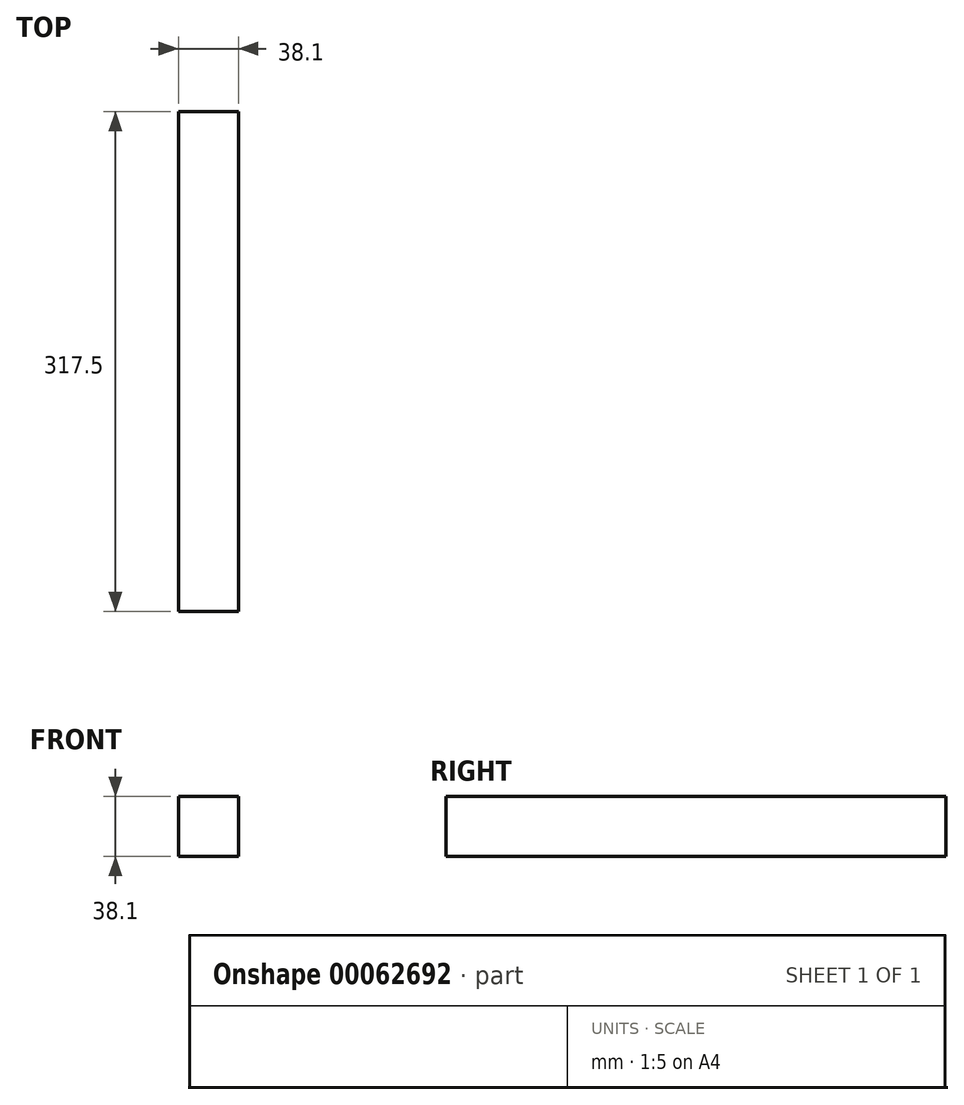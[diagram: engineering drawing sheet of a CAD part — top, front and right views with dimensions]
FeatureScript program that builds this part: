
annotation { "Feature Type Name" : "Feature", "Feature Type Description" : "" }
export const myFeature = defineFeature(function(context is Context, id is Id, definition is map)
    precondition{}
    {
        {
            var Q0;
            Q0=qCreatedBy(makeId("Front.planeOp"),FACE);
            var sketch = newSketch(context, id + "F0", { "sketchPlane" : qUnion([Q0])});
            skLineSegment(sketch, "E0.bottom", {"start": v(0, 0) * mm, "end": v(38.1, 0) * mm});
            skLineSegment(sketch, "E0.top", {"start": v(0, 38.1) * mm, "end": v(38.1, 38.1) * mm});
            skLineSegment(sketch, "E0.left", {"start": v(0, 0) * mm, "end": v(0, 38.1) * mm});
            skLineSegment(sketch, "E0.right", {"start": v(38.1, 0) * mm, "end": v(38.1, 38.1) * mm});
            skSolve(sketch);
        }
        {
            var Q0;
            Q0=makeQuery(id+"F0.imprint","IMPRINT",FACE,{"disambiguationData":[TD([[makeQuery(id+"F0.imprint","IMPRINT",EDGE,{"derivedFrom":sQuery(id+"F0.wireOp",EDGE,"E0.bottom")}),1.0]])]});
            extrude(context, id + "F1", {"entities" : qUnion([Q0]), "depth" : 317.5 * mm});
        }
    });
